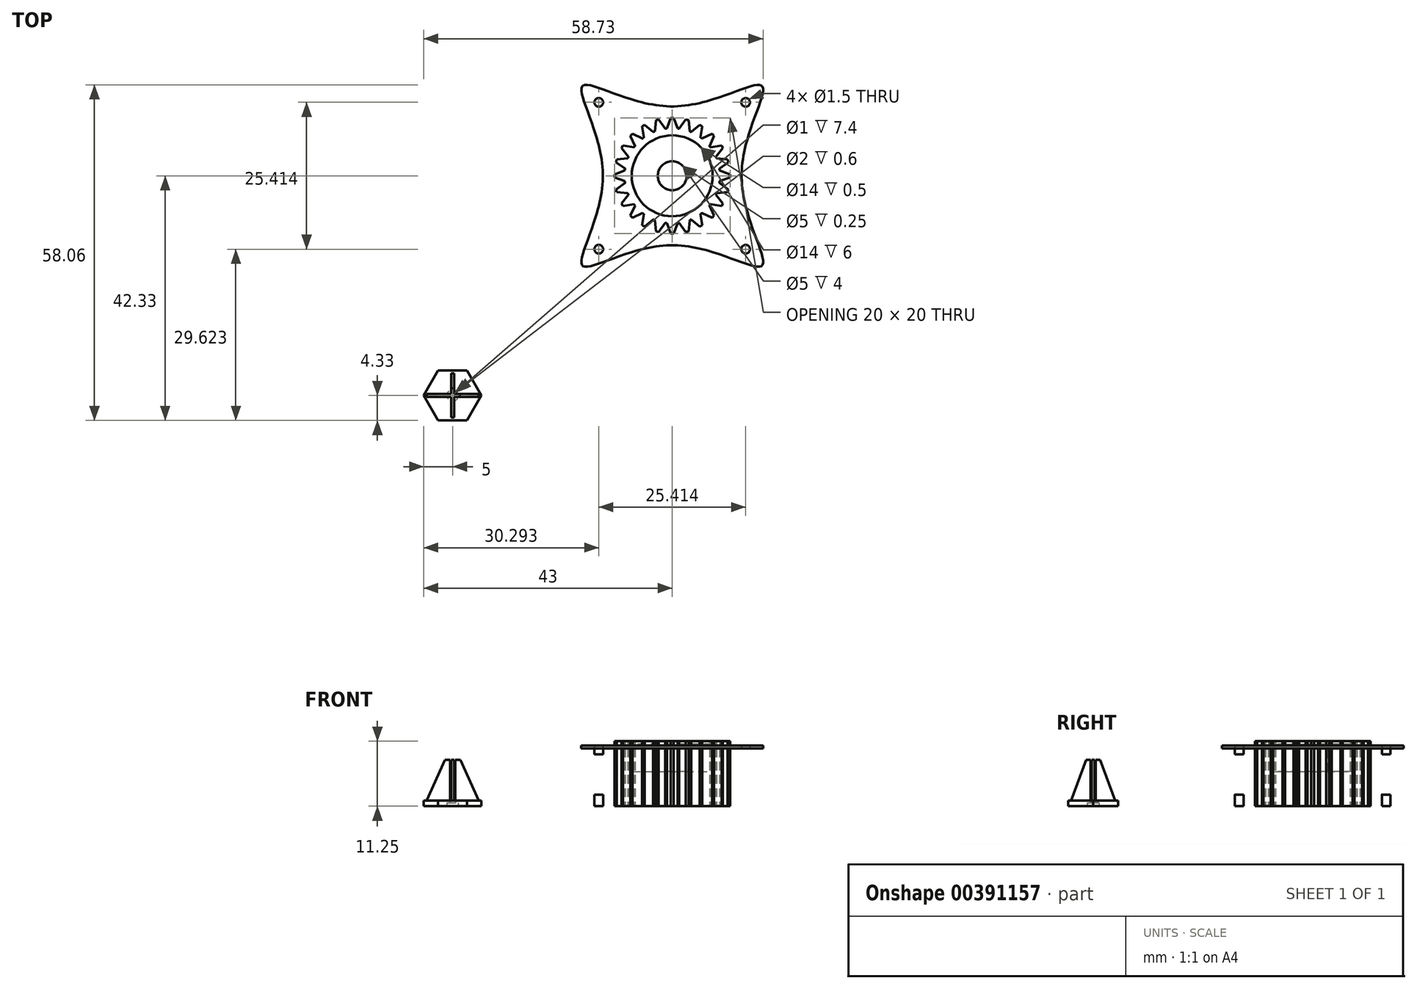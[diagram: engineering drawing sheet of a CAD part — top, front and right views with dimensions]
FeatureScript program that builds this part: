
annotation { "Feature Type Name" : "Feature", "Feature Type Description" : "" }
export const myFeature = defineFeature(function(context is Context, id is Id, definition is map)
    precondition{}
    {
        {
            var Q0;
            Q0=qCreatedBy(makeId("Top.planeOp"),FACE);
            var sketch = newSketch(context, id + "F0", { "sketchPlane" : qUnion([Q0])});
            skLineSegment(sketch, "E0.bottom", {"start": v(0, 0) * mm, "end": v(76, 0) * mm, "construction": true});
            skLineSegment(sketch, "E0.top", {"start": v(0, 76) * mm, "end": v(76, 76) * mm, "construction": true});
            skLineSegment(sketch, "E0.left", {"start": v(0, 0) * mm, "end": v(0, 76) * mm, "construction": true});
            skLineSegment(sketch, "E0.right", {"start": v(76, 0) * mm, "end": v(76, 76) * mm, "construction": true});
            skLineSegment(sketch, "E1", {"start": v(0, 0) * mm, "end": v(76, 76) * mm, "construction": true});
            skCircle(sketch, "E2", {"center": v(38, 38) * mm, "radius": 12 * mm, "construction": true});
            skLineSegment(sketch, "E3", {"start": v(0, 76) * mm, "end": v(76, 0) * mm, "construction": true});
            skLineSegment(sketch, "E4", {"start": v(38, 26) * mm, "end": v(50, 26) * mm, "construction": true});
            skLineSegment(sketch, "E5", {"start": v(50, 26) * mm, "end": v(50, 50) * mm, "construction": true});
            skLineSegment(sketch, "E6", {"start": v(50, 26) * mm, "end": v(53.54, 22.46) * mm, "construction": true});
            skLineSegment(sketch, "E7", {"start": v(53.54, 22.46) * mm, "end": v(53.54, 53.54) * mm, "construction": true});
            skLineSegment(sketch, "E8", {"start": v(53.54, 53.54) * mm, "end": v(22.46, 53.54) * mm, "construction": true});
            skLineSegment(sketch, "E9", {"start": v(22.46, 53.54) * mm, "end": v(22.46, 22.46) * mm, "construction": true});
            skLineSegment(sketch, "E10", {"start": v(22.46, 22.46) * mm, "end": v(53.54, 22.46) * mm, "construction": true});
            skPoint(sketch, "E11.7.internal.snap0", {"position": v(50, 38) * mm});
            skFitSpline(sketch, "E11", {"points": [v(22.46, 22.46) * mm, v(38, 26) * mm, v(53.54, 22.46) * mm, v(50, 38) * mm, v(53.54, 53.54) * mm, v(38, 50) * mm, v(22.46, 53.54) * mm, v(26, 38) * mm, v(22.46, 22.46) * mm]});
            skSolve(sketch);
        }
        {
            var Q0;
            Q0 = qSketchRegion(id + "F0", true);
            var Q1;
            Q1 = qConstructionFilter(qBodyType(qCreatedBy(id + "F0" ,EDGE), BodyType.WIRE), ConstructionObject.NO);
            extrude(context, id + "F1", {"entities" : qUnion([Q0]), "surfaceEntities" : qUnion([Q1]), "depth" : 2 * mm});
        }
        {
            var Q0;
            Q0=makeQuery(id+"F1.opExtrude","CAP_FACE",FACE,{"disambiguationData":[OSD([sQuery(id+"F0.wireOp",EDGE,"E11")])],"isStart":false});
            var sketch = newSketch(context, id + "F2", { "sketchPlane" : qUnion([Q0])});
            skLineSegment(sketch, "E12", {"start": v(0, 0) * mm, "end": v(38, 0) * mm, "construction": true});
            skLineSegment(sketch, "E13", {"start": v(38, 0) * mm, "end": v(38, 38) * mm, "construction": true});
            skCircle(sketch, "E14", {"center": v(38, 38) * mm, "radius": 10 * mm});
            skCircle(sketch, "E15", {"center": v(38, 38) * mm, "radius": 7 * mm});
            skLineSegment(sketch, "E16", {"start": v(38, 38) * mm, "end": v(22.46, 22.46) * mm, "construction": true});
            skLineSegment(sketch, "E17", {"start": v(30.94, 30.94) * mm, "end": v(31.3, 30.58) * mm, "construction": true});
            skLineSegment(sketch, "E18.MirrorCS", {"start": v(30.94, 30.94) * mm, "end": v(30.58, 31.3) * mm, "construction": true});
            skLineSegment(sketch, "E19", {"start": v(30.58, 31.3) * mm, "end": v(31.3, 30.58) * mm});
            skLineSegment(sketch, "E20", {"start": v(31.3, 30.58) * mm, "end": v(27.76, 27.05) * mm});
            skLineSegment(sketch, "E21", {"start": v(27.76, 27.05) * mm, "end": v(27.05, 27.76) * mm});
            skLineSegment(sketch, "E22", {"start": v(27.05, 27.76) * mm, "end": v(30.58, 31.3) * mm});
            skLineSegment(sketch, "E23", {"start": v(38, 38) * mm, "end": v(53.54, 22.46) * mm, "construction": true});
            skLineSegment(sketch, "E24", {"start": v(45.06, 30.94) * mm, "end": v(45.42, 31.3) * mm});
            skLineSegment(sketch, "E25", {"start": v(45.06, 30.94) * mm, "end": v(44.7, 30.58) * mm});
            skLineSegment(sketch, "E26", {"start": v(44.7, 30.58) * mm, "end": v(48.24, 27.05) * mm});
            skLineSegment(sketch, "E27", {"start": v(48.24, 27.05) * mm, "end": v(48.95, 27.76) * mm});
            skLineSegment(sketch, "E28", {"start": v(48.95, 27.76) * mm, "end": v(45.42, 31.3) * mm});
            skLineSegment(sketch, "E29", {"start": v(38, 38) * mm, "end": v(53.54, 53.54) * mm, "construction": true});
            skLineSegment(sketch, "E30", {"start": v(45.06, 45.06) * mm, "end": v(45.42, 44.7) * mm});
            skLineSegment(sketch, "E31", {"start": v(45.06, 45.06) * mm, "end": v(44.7, 45.42) * mm});
            skLineSegment(sketch, "E32", {"start": v(45.42, 44.7) * mm, "end": v(48.95, 48.24) * mm});
            skLineSegment(sketch, "E33", {"start": v(48.95, 48.24) * mm, "end": v(48.24, 48.95) * mm});
            skLineSegment(sketch, "E34", {"start": v(48.24, 48.95) * mm, "end": v(44.7, 45.42) * mm});
            skLineSegment(sketch, "E35", {"start": v(38, 38) * mm, "end": v(22.46, 53.54) * mm, "construction": true});
            skLineSegment(sketch, "E36", {"start": v(30.94, 45.06) * mm, "end": v(31.3, 45.42) * mm});
            skLineSegment(sketch, "E37", {"start": v(30.94, 45.06) * mm, "end": v(30.58, 44.7) * mm});
            skLineSegment(sketch, "E38", {"start": v(31.3, 45.42) * mm, "end": v(27.76, 48.95) * mm});
            skLineSegment(sketch, "E39", {"start": v(27.76, 48.95) * mm, "end": v(27.05, 48.24) * mm});
            skLineSegment(sketch, "E40", {"start": v(27.05, 48.24) * mm, "end": v(30.58, 44.7) * mm});
            skSolve(sketch);
        }
        {
            var Q0;
            Q0 = qSketchRegion(id + "F2", true);
            extrude(context, id + "F3", {"entities" : qUnion([Q0]), "operationType" : NewBodyOperationType.ADD, "depth" : 7 * mm});
        }
        {
            var Q0;
            Q0 = qSketchRegion(id + "F2", true);
            extrude(context, id + "F4", {"entities" : qUnion([Q0]), "operationType" : NewBodyOperationType.ADD, "depth" : 4 * mm});
        }
        {
            var Q0;
            Q0=makeQuery(id+"F3.opExtrude","SWEPT_FACE",FACE,{"disambiguationData":[OSD([sQuery(id+"F2.wireOp",EDGE,"E32")])]});
            var sketch = newSketch(context, id + "F5", { "sketchPlane" : qUnion([Q0])});
            skLineSegment(sketch, "E41", {"start": v(68.73, 2) * mm, "end": v(66.73, 2) * mm, "construction": true});
            skLineSegment(sketch, "E42", {"start": v(66.73, 2) * mm, "end": v(68.73, 9) * mm});
            skLineSegment(sketch, "E43", {"start": v(68.73, 9) * mm, "end": v(68.73, 2) * mm});
            skSolve(sketch);
        }
        {
            var Q0;
            {var subQ0=sQuery(id+"F5.wireOp",EDGE,"E42");Q0=makeQuery(id+"F5.imprint","IMPRINT",FACE,{"disambiguationData":[TD([[makeQuery(id+"F5.imprint","IMPRINT",EDGE,{"derivedFrom":subQ0}),-1.0]])]});}
            extrude(context, id + "F6", {"entities" : qUnion([Q0]), "operationType" : NewBodyOperationType.REMOVE, "oppositeDirection" : true, "depth" : 25 * mm});
        }
        {
            var Q0;
            Q0=makeQuery(id+"F3.opExtrude","SWEPT_FACE",FACE,{"disambiguationData":[OSD([sQuery(id+"F2.wireOp",EDGE,"E28")])]});
            var sketch = newSketch(context, id + "F7", { "sketchPlane" : qUnion([Q0])});
            skLineSegment(sketch, "E44", {"start": v(-14.99, 2) * mm, "end": v(-12.99, 2) * mm, "construction": true});
            skLineSegment(sketch, "E45", {"start": v(-12.99, 2) * mm, "end": v(-14.99, 9) * mm});
            skLineSegment(sketch, "E46", {"start": v(-14.99, 9) * mm, "end": v(-14.99, 2) * mm});
            skSolve(sketch);
        }
        {
            var Q0;
            {var subQ0=sQuery(id+"F7.wireOp",EDGE,"E45");Q0=makeQuery(id+"F7.imprint","IMPRINT",FACE,{"disambiguationData":[TD([[makeQuery(id+"F7.imprint","IMPRINT",EDGE,{"derivedFrom":subQ0}),1.0]])]});}
            extrude(context, id + "F8", {"entities" : qUnion([Q0]), "operationType" : NewBodyOperationType.REMOVE, "oppositeDirection" : true, "depth" : 25 * mm});
        }
        {
            var Q0;
            Q0=makeQuery(id+"F3.opExtrude","SWEPT_FACE",FACE,{"disambiguationData":[OSD([sQuery(id+"F2.wireOp",EDGE,"E38")])]});
            var sketch = newSketch(context, id + "F9", { "sketchPlane" : qUnion([Q0])});
            skLineSegment(sketch, "E47", {"start": v(14.99, 2) * mm, "end": v(12.99, 2) * mm, "construction": true});
            skLineSegment(sketch, "E48", {"start": v(12.99, 2) * mm, "end": v(14.99, 9) * mm});
            skLineSegment(sketch, "E49", {"start": v(14.99, 9) * mm, "end": v(14.99, 2) * mm});
            skSolve(sketch);
        }
        {
            var Q0;
            {var subQ0=sQuery(id+"F9.wireOp",EDGE,"E48");Q0=makeQuery(id+"F9.imprint","IMPRINT",FACE,{"disambiguationData":[TD([[makeQuery(id+"F9.imprint","IMPRINT",EDGE,{"derivedFrom":subQ0}),-1.0]])]});}
            extrude(context, id + "F10", {"entities" : qUnion([Q0]), "operationType" : NewBodyOperationType.REMOVE, "oppositeDirection" : true, "depth" : 25 * mm});
        }
        {
            var Q0;
            Q0=makeQuery(id+"F3.opExtrude","SWEPT_FACE",FACE,{"disambiguationData":[OSD([sQuery(id+"F2.wireOp",EDGE,"E22")])]});
            var sketch = newSketch(context, id + "F11", { "sketchPlane" : qUnion([Q0])});
            skLineSegment(sketch, "E50", {"start": v(-38.75, 2) * mm, "end": v(-40.75, 2) * mm, "construction": true});
            skLineSegment(sketch, "E51", {"start": v(-40.75, 2) * mm, "end": v(-38.75, 9) * mm});
            skLineSegment(sketch, "E52", {"start": v(-38.75, 9) * mm, "end": v(-38.75, 2) * mm});
            skSolve(sketch);
        }
        {
            var Q0;
            {var subQ0=sQuery(id+"F11.wireOp",EDGE,"E51");Q0=makeQuery(id+"F11.imprint","IMPRINT",FACE,{"disambiguationData":[TD([[makeQuery(id+"F11.imprint","IMPRINT",EDGE,{"derivedFrom":subQ0}),-1.0]])]});}
            extrude(context, id + "F12", {"entities" : qUnion([Q0]), "operationType" : NewBodyOperationType.REMOVE, "oppositeDirection" : true, "depth" : 25 * mm});
        }
        {
            var Q0;
            {var subQ0=sQuery(id+"F2.wireOp",EDGE,"E22");var subQ1=sQuery(id+"F2.wireOp",EDGE,"E38");var subQ2=sQuery(id+"F2.wireOp",EDGE,"E28");var subQ3=sQuery(id+"F2.wireOp",EDGE,"E32");var subQ7=sQuery(id+"F0.wireOp",EDGE,"E11");Q0=makeQuery(id+"F12.boolean.opBoolean","MERGE",FACE,{"derivedFrom":[makeQuery(id+"F10.boolean.opBoolean","MERGE",FACE,{"derivedFrom":[makeQuery(id+"F8.boolean.opBoolean","MERGE",FACE,{"derivedFrom":[makeQuery(id+"F6.boolean.opBoolean","MERGE",FACE,{"derivedFrom":[makeQuery(id+"F3.boolean.opBoolean","SPLIT",FACE,{"disambiguationData":[TD([makeQuery(id+"F1.opExtrude","SWEPT_FACE",FACE,{"disambiguationData":[OSD([subQ7])]})])],"derivedFrom":makeQuery(id+"F1.opExtrude","CAP_FACE",FACE,{"disambiguationData":[OSD([subQ7])],"isStart":false})}),makeQuery(id+"F6.opExtrude","SWEPT_FACE",FACE,{"disambiguationData":[OSD([subQ3])]})]}),makeQuery(id+"F8.opExtrude","SWEPT_FACE",FACE,{"disambiguationData":[OSD([subQ2])]})]}),makeQuery(id+"F10.opExtrude","SWEPT_FACE",FACE,{"disambiguationData":[OSD([subQ1])]})]}),makeQuery(id+"F12.opExtrude","SWEPT_FACE",FACE,{"disambiguationData":[OSD([subQ0])]})]});}
            var sketch = newSketch(context, id + "F13", { "sketchPlane" : qUnion([Q0])});
            skLineSegment(sketch, "E53", {"start": v(38, 38) * mm, "end": v(38, 26) * mm, "construction": true});
            skLineSegment(sketch, "E54", {"start": v(38, 38) * mm, "end": v(50, 38) * mm, "construction": true});
            skLineSegment(sketch, "E55", {"start": v(38, 38) * mm, "end": v(38, 50) * mm, "construction": true});
            skLineSegment(sketch, "E56", {"start": v(38, 38) * mm, "end": v(26, 38) * mm, "construction": true});
            skLineSegment(sketch, "E57", {"start": v(38, 38) * mm, "end": v(53.54, 22.46) * mm, "construction": true});
            skLineSegment(sketch, "E58", {"start": v(38, 38) * mm, "end": v(53.54, 53.54) * mm, "construction": true});
            skLineSegment(sketch, "E59", {"start": v(38, 38) * mm, "end": v(22.46, 53.54) * mm, "construction": true});
            skLineSegment(sketch, "E60", {"start": v(38, 38) * mm, "end": v(22.46, 22.46) * mm, "construction": true});
            skFitSpline(sketch, "E61", {"points": [v(38, 26) * mm, v(53.54, 22.46) * mm, v(50, 38) * mm, v(53.54, 53.54) * mm, v(38, 50) * mm, v(22.46, 53.54) * mm, v(26, 38) * mm, v(22.46, 22.46) * mm, v(38, 26) * mm]});
            skSolve(sketch);
        }
        {
            var Q0;
            Q0 = qSketchRegion(id + "F13", true);
            extrude(context, id + "F14", {"entities" : qUnion([Q0]), "operationType" : NewBodyOperationType.ADD, "depth" : 8 * mm, "hasSecondDirection" : true, "secondDirectionOppositeDirection" : false, "secondDirectionDepth" : 7 * mm});
        }
        {
            var Q0;
            Q0=makeQuery(id+"F14.opExtrude","CAP_FACE",FACE,{"disambiguationData":[OSD([sQuery(id+"F13.wireOp",EDGE,"E61")])],"isStart":false});
            var sketch = newSketch(context, id + "F15", { "sketchPlane" : qUnion([Q0])});
            skLineSegment(sketch, "E62", {"start": v(0, 0) * mm, "end": v(38, 0) * mm, "construction": true});
            skLineSegment(sketch, "E63", {"start": v(38, 0) * mm, "end": v(38, 38) * mm, "construction": true});
            skCircle(sketch, "E64", {"center": v(38, 38) * mm, "radius": 10 * mm, "construction": true});
            skLineSegment(sketch, "E65", {"start": v(38, 28) * mm, "end": v(38.25, 28) * mm});
            skLineSegment(sketch, "E66", {"start": v(37.75, 28) * mm, "end": v(38, 28) * mm});
            skLineSegment(sketch, "E67", {"start": v(38.93, 29.8) * mm, "end": v(38.25, 28) * mm});
            skLineSegment(sketch, "E68.MirrorCS", {"start": v(37.07, 29.8) * mm, "end": v(37.75, 28) * mm});
            skLineSegment(sketch, "E69.1.2", {"start": v(34.98, 30.32) * mm, "end": v(35.17, 28.4) * mm});
            skLineSegment(sketch, "E69.1.3", {"start": v(35.17, 28.4) * mm, "end": v(35.41, 28.34) * mm});
            skLineSegment(sketch, "E69.1.4", {"start": v(35.41, 28.34) * mm, "end": v(35.65, 28.28) * mm});
            skLineSegment(sketch, "E69.1.5", {"start": v(36.77, 29.84) * mm, "end": v(35.65, 28.28) * mm});
            skLineSegment(sketch, "E69.2.2", {"start": v(33.1, 31.36) * mm, "end": v(32.78, 29.46) * mm});
            skLineSegment(sketch, "E69.2.3", {"start": v(32.78, 29.46) * mm, "end": v(33, 29.34) * mm});
            skLineSegment(sketch, "E69.2.4", {"start": v(33, 29.34) * mm, "end": v(33.22, 29.21) * mm});
            skLineSegment(sketch, "E69.2.5", {"start": v(34.7, 30.44) * mm, "end": v(33.22, 29.21) * mm});
            skLineSegment(sketch, "E69.3.2", {"start": v(31.55, 32.86) * mm, "end": v(30.75, 31.1) * mm});
            skLineSegment(sketch, "E69.3.3", {"start": v(30.75, 31.1) * mm, "end": v(30.93, 30.93) * mm});
            skLineSegment(sketch, "E69.3.4", {"start": v(30.93, 30.93) * mm, "end": v(31.1, 30.75) * mm});
            skLineSegment(sketch, "E69.3.5", {"start": v(32.86, 31.55) * mm, "end": v(31.1, 30.75) * mm});
            skLineSegment(sketch, "E69.4.2", {"start": v(30.44, 34.7) * mm, "end": v(29.21, 33.22) * mm});
            skLineSegment(sketch, "E69.4.3", {"start": v(29.21, 33.22) * mm, "end": v(29.34, 33) * mm});
            skLineSegment(sketch, "E69.4.4", {"start": v(29.34, 33) * mm, "end": v(29.46, 32.78) * mm});
            skLineSegment(sketch, "E69.4.5", {"start": v(31.36, 33.1) * mm, "end": v(29.46, 32.78) * mm});
            skLineSegment(sketch, "E69.5.2", {"start": v(29.84, 36.77) * mm, "end": v(28.28, 35.65) * mm});
            skLineSegment(sketch, "E69.5.3", {"start": v(28.28, 35.65) * mm, "end": v(28.34, 35.41) * mm});
            skLineSegment(sketch, "E69.5.4", {"start": v(28.34, 35.41) * mm, "end": v(28.4, 35.17) * mm});
            skLineSegment(sketch, "E69.5.5", {"start": v(30.32, 34.98) * mm, "end": v(28.4, 35.17) * mm});
            skLineSegment(sketch, "E69.6.2", {"start": v(29.8, 38.93) * mm, "end": v(28, 38.25) * mm});
            skLineSegment(sketch, "E69.6.3", {"start": v(28, 38.25) * mm, "end": v(28, 38) * mm});
            skLineSegment(sketch, "E69.6.4", {"start": v(28, 38) * mm, "end": v(28, 37.75) * mm});
            skLineSegment(sketch, "E69.6.5", {"start": v(29.8, 37.07) * mm, "end": v(28, 37.75) * mm});
            skLineSegment(sketch, "E69.7.2", {"start": v(30.32, 41.02) * mm, "end": v(28.4, 40.83) * mm});
            skLineSegment(sketch, "E69.7.3", {"start": v(28.4, 40.83) * mm, "end": v(28.34, 40.59) * mm});
            skLineSegment(sketch, "E69.7.4", {"start": v(28.34, 40.59) * mm, "end": v(28.28, 40.35) * mm});
            skLineSegment(sketch, "E69.7.5", {"start": v(29.84, 39.23) * mm, "end": v(28.28, 40.35) * mm});
            skLineSegment(sketch, "E69.8.2", {"start": v(31.36, 42.9) * mm, "end": v(29.46, 43.22) * mm});
            skLineSegment(sketch, "E69.8.3", {"start": v(29.46, 43.22) * mm, "end": v(29.34, 43) * mm});
            skLineSegment(sketch, "E69.8.4", {"start": v(29.34, 43) * mm, "end": v(29.21, 42.78) * mm});
            skLineSegment(sketch, "E69.8.5", {"start": v(30.44, 41.3) * mm, "end": v(29.21, 42.78) * mm});
            skLineSegment(sketch, "E69.9.2", {"start": v(32.86, 44.45) * mm, "end": v(31.1, 45.25) * mm});
            skLineSegment(sketch, "E69.9.3", {"start": v(31.1, 45.25) * mm, "end": v(30.93, 45.07) * mm});
            skLineSegment(sketch, "E69.9.4", {"start": v(30.93, 45.07) * mm, "end": v(30.75, 44.9) * mm});
            skLineSegment(sketch, "E69.9.5", {"start": v(31.55, 43.14) * mm, "end": v(30.75, 44.9) * mm});
            skLineSegment(sketch, "E69.10.2", {"start": v(34.7, 45.56) * mm, "end": v(33.22, 46.79) * mm});
            skLineSegment(sketch, "E69.10.3", {"start": v(33.22, 46.79) * mm, "end": v(33, 46.66) * mm});
            skLineSegment(sketch, "E69.10.4", {"start": v(33, 46.66) * mm, "end": v(32.78, 46.54) * mm});
            skLineSegment(sketch, "E69.10.5", {"start": v(33.1, 44.64) * mm, "end": v(32.78, 46.54) * mm});
            skLineSegment(sketch, "E69.11.2", {"start": v(36.77, 46.16) * mm, "end": v(35.65, 47.72) * mm});
            skLineSegment(sketch, "E69.11.3", {"start": v(35.65, 47.72) * mm, "end": v(35.41, 47.66) * mm});
            skLineSegment(sketch, "E69.11.4", {"start": v(35.41, 47.66) * mm, "end": v(35.17, 47.6) * mm});
            skLineSegment(sketch, "E69.11.5", {"start": v(34.98, 45.68) * mm, "end": v(35.17, 47.6) * mm});
            skLineSegment(sketch, "E69.12.2", {"start": v(38.93, 46.2) * mm, "end": v(38.25, 48) * mm});
            skLineSegment(sketch, "E69.12.3", {"start": v(38.25, 48) * mm, "end": v(38, 48) * mm});
            skLineSegment(sketch, "E69.12.4", {"start": v(38, 48) * mm, "end": v(37.75, 48) * mm});
            skLineSegment(sketch, "E69.12.5", {"start": v(37.07, 46.2) * mm, "end": v(37.75, 48) * mm});
            skLineSegment(sketch, "E69.13.2", {"start": v(41.02, 45.68) * mm, "end": v(40.83, 47.6) * mm});
            skLineSegment(sketch, "E69.13.3", {"start": v(40.83, 47.6) * mm, "end": v(40.59, 47.66) * mm});
            skLineSegment(sketch, "E69.13.4", {"start": v(40.59, 47.66) * mm, "end": v(40.35, 47.72) * mm});
            skLineSegment(sketch, "E69.13.5", {"start": v(39.23, 46.16) * mm, "end": v(40.35, 47.72) * mm});
            skLineSegment(sketch, "E69.14.2", {"start": v(42.9, 44.64) * mm, "end": v(43.22, 46.54) * mm});
            skLineSegment(sketch, "E69.14.3", {"start": v(43.22, 46.54) * mm, "end": v(43, 46.66) * mm});
            skLineSegment(sketch, "E69.14.4", {"start": v(43, 46.66) * mm, "end": v(42.78, 46.79) * mm});
            skLineSegment(sketch, "E69.14.5", {"start": v(41.3, 45.56) * mm, "end": v(42.78, 46.79) * mm});
            skLineSegment(sketch, "E69.15.2", {"start": v(44.45, 43.14) * mm, "end": v(45.25, 44.9) * mm});
            skLineSegment(sketch, "E69.15.3", {"start": v(45.25, 44.9) * mm, "end": v(45.07, 45.07) * mm});
            skLineSegment(sketch, "E69.15.4", {"start": v(45.07, 45.07) * mm, "end": v(44.9, 45.25) * mm});
            skLineSegment(sketch, "E69.15.5", {"start": v(43.14, 44.45) * mm, "end": v(44.9, 45.25) * mm});
            skLineSegment(sketch, "E69.16.2", {"start": v(45.56, 41.3) * mm, "end": v(46.79, 42.78) * mm});
            skLineSegment(sketch, "E69.16.3", {"start": v(46.79, 42.78) * mm, "end": v(46.66, 43) * mm});
            skLineSegment(sketch, "E69.16.4", {"start": v(46.66, 43) * mm, "end": v(46.54, 43.22) * mm});
            skLineSegment(sketch, "E69.16.5", {"start": v(44.64, 42.9) * mm, "end": v(46.54, 43.22) * mm});
            skLineSegment(sketch, "E69.17.2", {"start": v(46.16, 39.23) * mm, "end": v(47.72, 40.35) * mm});
            skLineSegment(sketch, "E69.17.3", {"start": v(47.72, 40.35) * mm, "end": v(47.66, 40.59) * mm});
            skLineSegment(sketch, "E69.17.4", {"start": v(47.66, 40.59) * mm, "end": v(47.6, 40.83) * mm});
            skLineSegment(sketch, "E69.17.5", {"start": v(45.68, 41.02) * mm, "end": v(47.6, 40.83) * mm});
            skLineSegment(sketch, "E69.18.2", {"start": v(46.2, 37.07) * mm, "end": v(48, 37.75) * mm});
            skLineSegment(sketch, "E69.18.3", {"start": v(48, 37.75) * mm, "end": v(48, 38) * mm});
            skLineSegment(sketch, "E69.18.4", {"start": v(48, 38) * mm, "end": v(48, 38.25) * mm});
            skLineSegment(sketch, "E69.18.5", {"start": v(46.2, 38.93) * mm, "end": v(48, 38.25) * mm});
            skLineSegment(sketch, "E69.19.2", {"start": v(45.68, 34.98) * mm, "end": v(47.6, 35.17) * mm});
            skLineSegment(sketch, "E69.19.3", {"start": v(47.6, 35.17) * mm, "end": v(47.66, 35.41) * mm});
            skLineSegment(sketch, "E69.19.4", {"start": v(47.66, 35.41) * mm, "end": v(47.72, 35.65) * mm});
            skLineSegment(sketch, "E69.19.5", {"start": v(46.16, 36.77) * mm, "end": v(47.72, 35.65) * mm});
            skLineSegment(sketch, "E69.anchor1", {"start": v(38, 38) * mm, "end": v(38, 30) * mm, "construction": true});
            skLineSegment(sketch, "E69.anchor2", {"start": v(38, 38) * mm, "end": v(38, 30) * mm, "construction": true});
            skLineSegment(sketch, "E70.6.20.0", {"start": v(44.64, 33.1) * mm, "end": v(46.54, 32.78) * mm});
            skLineSegment(sketch, "E70.9.20.0", {"start": v(46.54, 32.78) * mm, "end": v(46.66, 33) * mm});
            skLineSegment(sketch, "E70.12.20.0", {"start": v(46.66, 33) * mm, "end": v(46.79, 33.22) * mm});
            skLineSegment(sketch, "E70.15.20.0", {"start": v(45.56, 34.7) * mm, "end": v(46.79, 33.22) * mm});
            skLineSegment(sketch, "E70.6.21.0", {"start": v(43.14, 31.55) * mm, "end": v(44.9, 30.75) * mm});
            skLineSegment(sketch, "E70.9.21.0", {"start": v(44.9, 30.75) * mm, "end": v(45.07, 30.93) * mm});
            skLineSegment(sketch, "E70.12.21.0", {"start": v(45.07, 30.93) * mm, "end": v(45.25, 31.1) * mm});
            skLineSegment(sketch, "E70.15.21.0", {"start": v(44.45, 32.86) * mm, "end": v(45.25, 31.1) * mm});
            skLineSegment(sketch, "E70.6.22.0", {"start": v(41.3, 30.44) * mm, "end": v(42.78, 29.21) * mm});
            skLineSegment(sketch, "E70.9.22.0", {"start": v(42.78, 29.21) * mm, "end": v(43, 29.34) * mm});
            skLineSegment(sketch, "E70.12.22.0", {"start": v(43, 29.34) * mm, "end": v(43.22, 29.46) * mm});
            skLineSegment(sketch, "E70.15.22.0", {"start": v(42.9, 31.36) * mm, "end": v(43.22, 29.46) * mm});
            skLineSegment(sketch, "E70.6.23.0", {"start": v(39.23, 29.84) * mm, "end": v(40.35, 28.28) * mm});
            skLineSegment(sketch, "E70.9.23.0", {"start": v(40.35, 28.28) * mm, "end": v(40.59, 28.34) * mm});
            skLineSegment(sketch, "E70.12.23.0", {"start": v(40.59, 28.34) * mm, "end": v(40.83, 28.4) * mm});
            skLineSegment(sketch, "E70.15.23.0", {"start": v(41.02, 30.32) * mm, "end": v(40.83, 28.4) * mm});
            skArc(sketch, "E71", {"start": v(34.7, 30.44) * mm, "mid": v(34.84, 30.38) * mm, "end": v(34.98, 30.32) * mm});
            skPoint(sketch, "E72.orphan", {"position": v(30, 37) * mm});
            skPoint(sketch, "E73.orphan", {"position": v(30.01, 36.9) * mm});
            skPoint(sketch, "E74.orphan", {"position": v(30.57, 34.87) * mm});
            skPoint(sketch, "E75.orphan", {"position": v(31.57, 33.13) * mm});
            skPoint(sketch, "E76.orphan", {"position": v(31.64, 33.05) * mm});
            skPoint(sketch, "E77.orphan", {"position": v(33.05, 31.64) * mm});
            skPoint(sketch, "E78.orphan", {"position": v(33.13, 31.57) * mm});
            skArc(sketch, "E79.trimOffspring", {"start": v(32.86, 31.55) * mm, "mid": v(32.98, 31.45) * mm, "end": v(33.1, 31.36) * mm});
            skArc(sketch, "E80.trimOffspring", {"start": v(31.36, 33.1) * mm, "mid": v(31.45, 32.98) * mm, "end": v(31.55, 32.86) * mm});
            skArc(sketch, "E81.trimOffspring", {"start": v(36.77, 29.84) * mm, "mid": v(36.92, 29.82) * mm, "end": v(37.07, 29.8) * mm});
            skPoint(sketch, "E82.orphan", {"position": v(36.9, 30.01) * mm});
            skPoint(sketch, "E83.orphan", {"position": v(37, 30) * mm});
            skPoint(sketch, "E84.MirrorCS.start.orphan", {"position": v(38, 30) * mm});
            skPoint(sketch, "E85.orphan", {"position": v(34.96, 30.53) * mm});
            skPoint(sketch, "E86.orphan", {"position": v(34.87, 30.57) * mm});
            skArc(sketch, "E87.trimOffspring", {"start": v(38.93, 29.8) * mm, "mid": v(39.08, 29.82) * mm, "end": v(39.23, 29.84) * mm});
            skArc(sketch, "E88.trimOffspring", {"start": v(30.32, 34.98) * mm, "mid": v(30.38, 34.84) * mm, "end": v(30.44, 34.7) * mm});
            skArc(sketch, "E89.trimOffspring", {"start": v(29.8, 37.07) * mm, "mid": v(29.82, 36.92) * mm, "end": v(29.84, 36.77) * mm});
            skArc(sketch, "E90.trimOffspring", {"start": v(41.02, 30.32) * mm, "mid": v(41.16, 30.38) * mm, "end": v(41.3, 30.44) * mm});
            skPoint(sketch, "E91.orphan", {"position": v(39.1, 30.01) * mm});
            skPoint(sketch, "E92.orphan", {"position": v(39, 30) * mm});
            skPoint(sketch, "E93.orphan", {"position": v(41.13, 30.57) * mm});
            skPoint(sketch, "E94.orphan", {"position": v(41.04, 30.53) * mm});
            skPoint(sketch, "E95.orphan", {"position": v(42.87, 31.57) * mm});
            skPoint(sketch, "E96.orphan", {"position": v(42.95, 31.64) * mm});
            skPoint(sketch, "E97.orphan", {"position": v(44.36, 33.05) * mm});
            skPoint(sketch, "E98.orphan", {"position": v(44.43, 33.13) * mm});
            skPoint(sketch, "E99.orphan", {"position": v(45.43, 34.87) * mm});
            skPoint(sketch, "E100.orphan", {"position": v(45.47, 34.96) * mm});
            skPoint(sketch, "E101.orphan", {"position": v(45.99, 36.9) * mm});
            skPoint(sketch, "E102.orphan", {"position": v(46, 37) * mm});
            skPoint(sketch, "E103.orphan", {"position": v(46, 39) * mm});
            skPoint(sketch, "E104.orphan", {"position": v(45.99, 39.1) * mm});
            skPoint(sketch, "E105.orphan", {"position": v(45.47, 41.04) * mm});
            skPoint(sketch, "E106.orphan", {"position": v(45.43, 41.13) * mm});
            skPoint(sketch, "E107.orphan", {"position": v(44.43, 42.87) * mm});
            skPoint(sketch, "E108.orphan", {"position": v(44.36, 42.95) * mm});
            skPoint(sketch, "E109.orphan", {"position": v(42.95, 44.36) * mm});
            skPoint(sketch, "E110.orphan", {"position": v(42.87, 44.43) * mm});
            skArc(sketch, "E111.trimOffspring", {"start": v(44.45, 32.86) * mm, "mid": v(44.55, 32.98) * mm, "end": v(44.64, 33.1) * mm});
            skArc(sketch, "E112.trimOffspring", {"start": v(46.16, 36.77) * mm, "mid": v(46.18, 36.92) * mm, "end": v(46.2, 37.07) * mm});
            skArc(sketch, "E113.trimOffspring", {"start": v(45.68, 41.02) * mm, "mid": v(45.62, 41.16) * mm, "end": v(45.56, 41.3) * mm});
            skArc(sketch, "E114.trimOffspring", {"start": v(44.64, 42.9) * mm, "mid": v(44.55, 43.02) * mm, "end": v(44.45, 43.14) * mm});
            skArc(sketch, "E115.trimOffspring", {"start": v(46.2, 38.93) * mm, "mid": v(46.18, 39.08) * mm, "end": v(46.16, 39.23) * mm});
            skArc(sketch, "E116.trimOffspring", {"start": v(43.14, 44.45) * mm, "mid": v(43.02, 44.55) * mm, "end": v(42.9, 44.64) * mm});
            skArc(sketch, "E117.trimOffspring", {"start": v(41.3, 45.56) * mm, "mid": v(41.16, 45.62) * mm, "end": v(41.02, 45.68) * mm});
            skPoint(sketch, "E118.orphan", {"position": v(41.04, 45.47) * mm});
            skArc(sketch, "E119.trimOffspring", {"start": v(39.23, 46.16) * mm, "mid": v(39.08, 46.18) * mm, "end": v(38.93, 46.2) * mm});
            skPoint(sketch, "E120.orphan", {"position": v(39.1, 45.99) * mm});
            skPoint(sketch, "E121.orphan", {"position": v(39, 46) * mm});
            skArc(sketch, "E122.trimOffspring", {"start": v(37.07, 46.2) * mm, "mid": v(36.92, 46.18) * mm, "end": v(36.77, 46.16) * mm});
            skPoint(sketch, "E123.orphan", {"position": v(37, 46) * mm});
            skPoint(sketch, "E124.orphan", {"position": v(36.9, 45.99) * mm});
            skArc(sketch, "E125.trimOffspring", {"start": v(34.98, 45.68) * mm, "mid": v(34.84, 45.62) * mm, "end": v(34.7, 45.56) * mm});
            skPoint(sketch, "E126.orphan", {"position": v(34.96, 45.47) * mm});
            skPoint(sketch, "E127.orphan", {"position": v(34.87, 45.43) * mm});
            skPoint(sketch, "E128.orphan", {"position": v(33.13, 44.43) * mm});
            skPoint(sketch, "E129.orphan", {"position": v(33.05, 44.36) * mm});
            skPoint(sketch, "E130.orphan", {"position": v(31.64, 42.95) * mm});
            skPoint(sketch, "E131.orphan", {"position": v(31.57, 42.87) * mm});
            skArc(sketch, "E132.trimOffspring", {"start": v(33.1, 44.64) * mm, "mid": v(32.98, 44.55) * mm, "end": v(32.86, 44.45) * mm});
            skArc(sketch, "E133.trimOffspring", {"start": v(31.55, 43.14) * mm, "mid": v(31.45, 43.02) * mm, "end": v(31.36, 42.9) * mm});
            skArc(sketch, "E134.trimOffspring", {"start": v(30.44, 41.3) * mm, "mid": v(30.38, 41.16) * mm, "end": v(30.32, 41.02) * mm});
            skPoint(sketch, "E135.orphan", {"position": v(30.57, 41.13) * mm});
            skPoint(sketch, "E136.orphan", {"position": v(30.53, 41.04) * mm});
            skArc(sketch, "E137.trimOffspring", {"start": v(29.84, 39.23) * mm, "mid": v(29.82, 39.08) * mm, "end": v(29.8, 38.93) * mm});
            skPoint(sketch, "E138.orphan", {"position": v(30, 39) * mm});
            skPoint(sketch, "E139.orphan", {"position": v(30.01, 39.1) * mm});
            skArc(sketch, "E140", {"start": v(42.9, 31.36) * mm, "mid": v(43.02, 31.45) * mm, "end": v(43.14, 31.55) * mm});
            skArc(sketch, "E141", {"start": v(45.56, 34.7) * mm, "mid": v(45.62, 34.84) * mm, "end": v(45.68, 34.98) * mm});
            skSolve(sketch);
        }
        {
            var Q0;
            Q0=makeQuery(id+"F15.imprint","IMPRINT",FACE,{"disambiguationData":[TD([[makeQuery(id+"F15.imprint","IMPRINT",EDGE,{"derivedFrom":sQuery(id+"F15.wireOp",EDGE,"E69.1.2")}),1.0]])]});
            extrude(context, id + "F16", {"entities" : qUnion([Q0]), "operationType" : NewBodyOperationType.ADD, "depth" : 1.25 * mm});
        }
        {
            var Q0;
            Q0=makeQuery(id+"F16.opExtrude","CAP_FACE",FACE,{"disambiguationData":[OSD([sQuery(id+"F15.wireOp",EDGE,"E69.1.2"),sQuery(id+"F15.wireOp",EDGE,"E69.1.3"),sQuery(id+"F15.wireOp",EDGE,"E69.1.4"),sQuery(id+"F15.wireOp",EDGE,"E69.1.5"),sQuery(id+"F15.wireOp",EDGE,"E69.2.2"),sQuery(id+"F15.wireOp",EDGE,"E69.2.3"),sQuery(id+"F15.wireOp",EDGE,"E69.2.4"),sQuery(id+"F15.wireOp",EDGE,"E69.2.5"),sQuery(id+"F15.wireOp",EDGE,"E69.3.2"),sQuery(id+"F15.wireOp",EDGE,"E69.3.3"),sQuery(id+"F15.wireOp",EDGE,"E69.3.4"),sQuery(id+"F15.wireOp",EDGE,"E69.3.5"),sQuery(id+"F15.wireOp",EDGE,"E69.4.2"),sQuery(id+"F15.wireOp",EDGE,"E69.4.3"),sQuery(id+"F15.wireOp",EDGE,"E69.4.4"),sQuery(id+"F15.wireOp",EDGE,"E69.4.5"),sQuery(id+"F15.wireOp",EDGE,"E69.5.2"),sQuery(id+"F15.wireOp",EDGE,"E69.5.3"),sQuery(id+"F15.wireOp",EDGE,"E69.5.4"),sQuery(id+"F15.wireOp",EDGE,"E69.5.5"),sQuery(id+"F15.wireOp",EDGE,"E69.6.2"),sQuery(id+"F15.wireOp",EDGE,"E69.6.3"),sQuery(id+"F15.wireOp",EDGE,"E69.6.4"),sQuery(id+"F15.wireOp",EDGE,"E69.6.5"),sQuery(id+"F15.wireOp",EDGE,"E69.7.2"),sQuery(id+"F15.wireOp",EDGE,"E69.7.3"),sQuery(id+"F15.wireOp",EDGE,"E69.7.4"),sQuery(id+"F15.wireOp",EDGE,"E69.7.5"),sQuery(id+"F15.wireOp",EDGE,"E69.8.2"),sQuery(id+"F15.wireOp",EDGE,"E69.8.3"),sQuery(id+"F15.wireOp",EDGE,"E69.8.4"),sQuery(id+"F15.wireOp",EDGE,"E69.8.5"),sQuery(id+"F15.wireOp",EDGE,"E69.9.2"),sQuery(id+"F15.wireOp",EDGE,"E69.9.3"),sQuery(id+"F15.wireOp",EDGE,"E69.9.4"),sQuery(id+"F15.wireOp",EDGE,"E69.9.5"),sQuery(id+"F15.wireOp",EDGE,"E69.10.2"),sQuery(id+"F15.wireOp",EDGE,"E69.10.3"),sQuery(id+"F15.wireOp",EDGE,"E69.10.4"),sQuery(id+"F15.wireOp",EDGE,"E69.10.5"),sQuery(id+"F15.wireOp",EDGE,"E69.11.2"),sQuery(id+"F15.wireOp",EDGE,"E69.11.3"),sQuery(id+"F15.wireOp",EDGE,"E69.11.4"),sQuery(id+"F15.wireOp",EDGE,"E69.11.5"),sQuery(id+"F15.wireOp",EDGE,"E69.12.2"),sQuery(id+"F15.wireOp",EDGE,"E69.12.3"),sQuery(id+"F15.wireOp",EDGE,"E69.12.4"),sQuery(id+"F15.wireOp",EDGE,"E69.12.5"),sQuery(id+"F15.wireOp",EDGE,"E69.13.2"),sQuery(id+"F15.wireOp",EDGE,"E69.13.3"),sQuery(id+"F15.wireOp",EDGE,"E69.13.4"),sQuery(id+"F15.wireOp",EDGE,"E69.13.5"),sQuery(id+"F15.wireOp",EDGE,"E69.14.2"),sQuery(id+"F15.wireOp",EDGE,"E69.14.3"),sQuery(id+"F15.wireOp",EDGE,"E69.14.4"),sQuery(id+"F15.wireOp",EDGE,"E69.14.5"),sQuery(id+"F15.wireOp",EDGE,"E69.15.2"),sQuery(id+"F15.wireOp",EDGE,"E69.15.3"),sQuery(id+"F15.wireOp",EDGE,"E69.15.4"),sQuery(id+"F15.wireOp",EDGE,"E69.15.5"),sQuery(id+"F15.wireOp",EDGE,"E69.16.2"),sQuery(id+"F15.wireOp",EDGE,"E69.16.3"),sQuery(id+"F15.wireOp",EDGE,"E69.16.4"),sQuery(id+"F15.wireOp",EDGE,"E69.16.5"),sQuery(id+"F15.wireOp",EDGE,"E69.17.2"),sQuery(id+"F15.wireOp",EDGE,"E69.17.3"),sQuery(id+"F15.wireOp",EDGE,"E69.17.4"),sQuery(id+"F15.wireOp",EDGE,"E69.17.5"),sQuery(id+"F15.wireOp",EDGE,"E69.18.2"),sQuery(id+"F15.wireOp",EDGE,"E69.18.3"),sQuery(id+"F15.wireOp",EDGE,"E69.18.4"),sQuery(id+"F15.wireOp",EDGE,"E69.18.5"),sQuery(id+"F15.wireOp",EDGE,"E69.19.2"),sQuery(id+"F15.wireOp",EDGE,"E69.19.3"),sQuery(id+"F15.wireOp",EDGE,"E69.19.4"),sQuery(id+"F15.wireOp",EDGE,"E69.19.5"),sQuery(id+"F15.wireOp",EDGE,"E70.6.20.0"),sQuery(id+"F15.wireOp",EDGE,"E70.9.20.0"),sQuery(id+"F15.wireOp",EDGE,"E70.12.20.0"),sQuery(id+"F15.wireOp",EDGE,"E70.15.20.0"),sQuery(id+"F15.wireOp",EDGE,"E70.6.21.0"),sQuery(id+"F15.wireOp",EDGE,"E70.9.21.0"),sQuery(id+"F15.wireOp",EDGE,"E70.12.21.0"),sQuery(id+"F15.wireOp",EDGE,"E70.15.21.0"),sQuery(id+"F15.wireOp",EDGE,"E70.6.22.0"),sQuery(id+"F15.wireOp",EDGE,"E70.9.22.0"),sQuery(id+"F15.wireOp",EDGE,"E70.12.22.0"),sQuery(id+"F15.wireOp",EDGE,"E70.15.22.0"),sQuery(id+"F15.wireOp",EDGE,"E70.6.23.0"),sQuery(id+"F15.wireOp",EDGE,"E70.9.23.0"),sQuery(id+"F15.wireOp",EDGE,"E70.12.23.0"),sQuery(id+"F15.wireOp",EDGE,"E70.15.23.0"),sQuery(id+"F15.wireOp",EDGE,"E68.MirrorCS"),sQuery(id+"F15.wireOp",EDGE,"E66"),sQuery(id+"F15.wireOp",EDGE,"E65"),sQuery(id+"F15.wireOp",EDGE,"E67"),sQuery(id+"F15.wireOp",EDGE,"E71"),sQuery(id+"F15.wireOp",EDGE,"E79.trimOffspring"),sQuery(id+"F15.wireOp",EDGE,"E80.trimOffspring"),sQuery(id+"F15.wireOp",EDGE,"E81.trimOffspring"),sQuery(id+"F15.wireOp",EDGE,"E87.trimOffspring"),sQuery(id+"F15.wireOp",EDGE,"E88.trimOffspring"),sQuery(id+"F15.wireOp",EDGE,"E89.trimOffspring"),sQuery(id+"F15.wireOp",EDGE,"E90.trimOffspring"),sQuery(id+"F15.wireOp",EDGE,"E111.trimOffspring"),sQuery(id+"F15.wireOp",EDGE,"E112.trimOffspring"),sQuery(id+"F15.wireOp",EDGE,"E113.trimOffspring"),sQuery(id+"F15.wireOp",EDGE,"E114.trimOffspring"),sQuery(id+"F15.wireOp",EDGE,"E115.trimOffspring"),sQuery(id+"F15.wireOp",EDGE,"E116.trimOffspring"),sQuery(id+"F15.wireOp",EDGE,"E117.trimOffspring"),sQuery(id+"F15.wireOp",EDGE,"E119.trimOffspring"),sQuery(id+"F15.wireOp",EDGE,"E122.trimOffspring"),sQuery(id+"F15.wireOp",EDGE,"E125.trimOffspring"),sQuery(id+"F15.wireOp",EDGE,"E132.trimOffspring"),sQuery(id+"F15.wireOp",EDGE,"E133.trimOffspring"),sQuery(id+"F15.wireOp",EDGE,"E134.trimOffspring"),sQuery(id+"F15.wireOp",EDGE,"E137.trimOffspring"),sQuery(id+"F15.wireOp",EDGE,"E140"),sQuery(id+"F15.wireOp",EDGE,"E141")])],"isStart":false});
            var sketch = newSketch(context, id + "F17", { "sketchPlane" : qUnion([Q0])});
            skCircle(sketch, "E142", {"center": v(38, 38) * mm, "radius": 7 * mm});
            skSolve(sketch);
        }
        {
            var Q0;
            Q0=makeQuery(id+"F17.imprint","IMPRINT",FACE,{"disambiguationData":[TD([[makeQuery(id+"F17.imprint","IMPRINT",EDGE,{"derivedFrom":sQuery(id+"F17.wireOp",EDGE,"E142")}),1.0]])]});
            extrude(context, id + "F18", {"entities" : qUnion([Q0]), "operationType" : NewBodyOperationType.REMOVE, "oppositeDirection" : true, "depth" : 0.5 * mm});
        }
        {
            var Q0;
            Q0=makeQuery(id+"F18.boolean.opBoolean","COPY",FACE,{"derivedFrom":makeQuery(id+"F18.opExtrude","CAP_FACE",FACE,{"disambiguationData":[OSD([sQuery(id+"F17.wireOp",EDGE,"E142")])],"isStart":false})});
            var sketch = newSketch(context, id + "F19", { "sketchPlane" : qUnion([Q0])});
            skCircle(sketch, "E143", {"center": v(38, 38) * mm, "radius": 2.5 * mm});
            skSolve(sketch);
        }
        {
            var Q0;
            Q0=makeQuery(id+"F19.imprint","IMPRINT",FACE,{"disambiguationData":[TD([[makeQuery(id+"F19.imprint","IMPRINT",EDGE,{"derivedFrom":sQuery(id+"F19.wireOp",EDGE,"E143")}),1.0]])]});
            extrude(context, id + "F20", {"entities" : qUnion([Q0]), "operationType" : NewBodyOperationType.REMOVE, "oppositeDirection" : true, "depth" : 25 * mm});
        }
        {
            var Q0;
            Q0=makeQuery(id+"F1.opExtrude","CAP_FACE",FACE,{"disambiguationData":[OSD([sQuery(id+"F0.wireOp",EDGE,"E11")])],"isStart":true});
            var sketch = newSketch(context, id + "F21", { "sketchPlane" : qUnion([Q0])});
            skCircle(sketch, "E144", {"center": v(38, -38) * mm, "radius": 7 * mm});
            skSolve(sketch);
        }
        {
            var Q0;
            Q0 = qSketchRegion(id + "F21", true);
            extrude(context, id + "F22", {"entities" : qUnion([Q0]), "operationType" : NewBodyOperationType.REMOVE, "oppositeDirection" : true, "depth" : 4 * mm});
        }
        {
            var Q0;
            Q0=makeQuery(id+"F14.boolean.opBoolean","SPLIT",FACE,{"disambiguationData":[TD([makeQuery(id+"F3.opExtrude","SWEPT_FACE",FACE,{"disambiguationData":[OSD([sQuery(id+"F2.wireOp",EDGE,"E15")])]})])],"derivedFrom":makeQuery(id+"F14.opExtrude","CAP_FACE",FACE,{"disambiguationData":[OSD([sQuery(id+"F13.wireOp",EDGE,"E61")])],"isStart":true})});
            var sketch = newSketch(context, id + "F23", { "sketchPlane" : qUnion([Q0])});
            skCircle(sketch, "E145", {"center": v(38, -38) * mm, "radius": 7 * mm});
            skCircle(sketch, "E146", {"center": v(38, -38) * mm, "radius": 2.5 * mm});
            skSolve(sketch);
        }
        {
            var Q0;
            Q0=makeQuery(id+"F23.imprint","IMPRINT",FACE,{"disambiguationData":[TD([[makeQuery(id+"F23.imprint","IMPRINT",EDGE,{"derivedFrom":sQuery(id+"F23.wireOp",EDGE,"E145")}),-1.0]])]});
            extrude(context, id + "F24", {"entities" : qUnion([Q0]), "operationType" : NewBodyOperationType.ADD, "depth" : 3 * mm});
        }
        {
            var Q0;
            Q0=makeQuery(id+"F14.opExtrude","CAP_FACE",FACE,{"disambiguationData":[OSD([sQuery(id+"F13.wireOp",EDGE,"E61")])],"isStart":false});
            var sketch = newSketch(context, id + "F25", { "sketchPlane" : qUnion([Q0])});
            skLineSegment(sketch, "E147", {"start": v(38, 38) * mm, "end": v(38, 15.14) * mm, "construction": true});
            skLineSegment(sketch, "E148", {"start": v(38, 38) * mm, "end": v(60.5, 15.5) * mm, "construction": true});
            skLineSegment(sketch, "E149", {"start": v(38, 38) * mm, "end": v(56.64, 56.64) * mm, "construction": true});
            skLineSegment(sketch, "E150", {"start": v(38, 38) * mm, "end": v(20.24, 55.76) * mm, "construction": true});
            skLineSegment(sketch, "E151", {"start": v(38, 38) * mm, "end": v(16.33, 16.33) * mm, "construction": true});
            skLineSegment(sketch, "E152", {"start": v(53.54, 53.54) * mm, "end": v(50.7, 50.7) * mm, "construction": true});
            skCircle(sketch, "E153", {"center": v(50.7, 50.7) * mm, "radius": 0.75 * mm});
            skCircle(sketch, "E154.MirrorC", {"center": v(25.3, 25.3) * mm, "radius": 0.75 * mm});
            skLineSegment(sketch, "E155", {"start": v(53.54, 22.46) * mm, "end": v(50.7, 25.3) * mm, "construction": true});
            skCircle(sketch, "E156", {"center": v(50.7, 25.3) * mm, "radius": 0.75 * mm});
            skCircle(sketch, "E157.MirrorC", {"center": v(25.3, 50.7) * mm, "radius": 0.75 * mm});
            skSolve(sketch);
        }
        {
            var Q0;
            Q0=makeQuery(id+"F25.imprint","IMPRINT",FACE,{"disambiguationData":[TD([[makeQuery(id+"F25.imprint","IMPRINT",EDGE,{"derivedFrom":sQuery(id+"F25.wireOp",EDGE,"E157.MirrorC")}),-1.0]])]});
            var Q1;
            Q1=makeQuery(id+"F25.imprint","IMPRINT",FACE,{"disambiguationData":[TD([[makeQuery(id+"F25.imprint","IMPRINT",EDGE,{"derivedFrom":sQuery(id+"F25.wireOp",EDGE,"E154.MirrorC")}),-1.0]])]});
            var Q2;
            Q2=makeQuery(id+"F25.imprint","IMPRINT",FACE,{"disambiguationData":[TD([[makeQuery(id+"F25.imprint","IMPRINT",EDGE,{"derivedFrom":sQuery(id+"F25.wireOp",EDGE,"E156")}),1.0]])]});
            var Q3;
            Q3=makeQuery(id+"F25.imprint","IMPRINT",FACE,{"disambiguationData":[TD([[makeQuery(id+"F25.imprint","IMPRINT",EDGE,{"derivedFrom":sQuery(id+"F25.wireOp",EDGE,"E153")}),1.0]])]});
            extrude(context, id + "F26", {"entities" : qUnion([Q0, Q1, Q2, Q3]), "operationType" : NewBodyOperationType.REMOVE, "oppositeDirection" : true, "depth" : 25 * mm});
        }
        {
            var Q0;
            Q0=makeQuery(id+"F14.opExtrude","CAP_FACE",FACE,{"disambiguationData":[OSD([sQuery(id+"F13.wireOp",EDGE,"E61")])],"isStart":false});
            var sketch = newSketch(context, id + "F27", { "sketchPlane" : qUnion([Q0])});
            skLineSegment(sketch, "E158", {"start": v(38, 38) * mm, "end": v(50.7, 25.3) * mm, "construction": true});
            skLineSegment(sketch, "E159", {"start": v(50.7, 25.3) * mm, "end": v(56.9, 19.1) * mm, "construction": true});
            skLineSegment(sketch, "E160", {"start": v(38, 38) * mm, "end": v(55.45, 55.45) * mm, "construction": true});
            skLineSegment(sketch, "E161", {"start": v(38, 38) * mm, "end": v(19.53, 56.47) * mm, "construction": true});
            skLineSegment(sketch, "E162", {"start": v(38, 38) * mm, "end": v(19.78, 19.78) * mm, "construction": true});
            skLineSegment(sketch, "E163", {"start": v(38, 38) * mm, "end": v(50, 38) * mm, "construction": true});
            skLineSegment(sketch, "E164", {"start": v(38, 38) * mm, "end": v(38, 50) * mm, "construction": true});
            skLineSegment(sketch, "E165", {"start": v(38, 38) * mm, "end": v(26, 38) * mm, "construction": true});
            skLineSegment(sketch, "E166", {"start": v(38, 38) * mm, "end": v(38, 26) * mm, "construction": true});
            skFitSpline(sketch, "E167", {"points": [v(53.54, 53.54) * mm, v(38, 50) * mm, v(22.46, 53.54) * mm, v(26, 38) * mm, v(22.46, 22.46) * mm, v(38, 26) * mm, v(53.54, 22.46) * mm, v(50, 38) * mm, v(53.54, 53.54) * mm]});
            skLineSegment(sketch, "E168", {"start": v(50.7, 50.7) * mm, "end": v(48.59, 48.59) * mm, "construction": true});
            skLineSegment(sketch, "E169", {"start": v(53.54, 53.54) * mm, "end": v(58, 49.06) * mm, "construction": true});
            skArc(sketch, "E170", {"start": v(30.96, 51.21) * mm, "mid": v(27.41, 48.59) * mm, "end": v(24.79, 45.04) * mm});
            skArc(sketch, "E171.trimOffspring", {"start": v(51.21, 45.04) * mm, "mid": v(48.59, 48.59) * mm, "end": v(45.04, 51.21) * mm});
            skArc(sketch, "E172.trimOffspring", {"start": v(45.04, 24.79) * mm, "mid": v(48.59, 27.41) * mm, "end": v(51.21, 30.96) * mm});
            skArc(sketch, "E173.trimOffspring", {"start": v(24.79, 30.96) * mm, "mid": v(27.41, 27.41) * mm, "end": v(30.96, 24.79) * mm});
            skCircle(sketch, "E174", {"center": v(50.7, 50.7) * mm, "radius": 0.75 * mm});
            skCircle(sketch, "E175", {"center": v(50.7, 25.3) * mm, "radius": 0.75 * mm});
            skCircle(sketch, "E176", {"center": v(25.3, 25.3) * mm, "radius": 0.75 * mm});
            skCircle(sketch, "E177", {"center": v(25.3, 50.7) * mm, "radius": 0.75 * mm});
            skSolve(sketch);
        }
        {
            var Q0;
            Q0 = qSketchRegion(id + "F27", true);
            extrude(context, id + "F28", {"entities" : qUnion([Q0]), "operationType" : NewBodyOperationType.ADD, "depth" : 0.5 * mm});
        }
        {
            var Q0;
            Q0=qCreatedBy(makeId("Top.planeOp"),FACE);
            var sketch = newSketch(context, id + "F29", { "sketchPlane" : qUnion([Q0])});
            skCircle(sketch, "E178.cCircle", {"center": v(0, 0) * mm, "radius": 5 * mm, "construction": true});
            skLineSegment(sketch, "E178.0", {"start": v(5, 0) * mm, "end": v(2.5, -4.33) * mm});
            skLineSegment(sketch, "E178.1", {"start": v(2.5, -4.33) * mm, "end": v(-2.5, -4.33) * mm});
            skLineSegment(sketch, "E178.2", {"start": v(-2.5, -4.33) * mm, "end": v(-5, 0) * mm});
            skLineSegment(sketch, "E178.3", {"start": v(-5, 0) * mm, "end": v(-2.5, 4.33) * mm});
            skLineSegment(sketch, "E178.4", {"start": v(-2.5, 4.33) * mm, "end": v(2.5, 4.33) * mm});
            skLineSegment(sketch, "E178.5", {"start": v(2.5, 4.33) * mm, "end": v(5, 0) * mm});
            skSolve(sketch);
        }
        {
            var Q0;
            Q0 = qSketchRegion(id + "F29", true);
            extrude(context, id + "F30", {"entities" : qUnion([Q0]), "depth" : 1 * mm});
        }
        {
            var Q0;
            Q0=makeQuery(id+"F30.opExtrude","CAP_FACE",FACE,{"disambiguationData":[OSD([sQuery(id+"F29.wireOp",EDGE,"E178.0"),sQuery(id+"F29.wireOp",EDGE,"E178.1"),sQuery(id+"F29.wireOp",EDGE,"E178.2"),sQuery(id+"F29.wireOp",EDGE,"E178.3"),sQuery(id+"F29.wireOp",EDGE,"E178.4"),sQuery(id+"F29.wireOp",EDGE,"E178.5")])],"isStart":false});
            var sketch = newSketch(context, id + "F31", { "sketchPlane" : qUnion([Q0])});
            skLineSegment(sketch, "E179", {"start": v(0, 4.33) * mm, "end": v(0, 3.83) * mm, "construction": true});
            skLineSegment(sketch, "E180", {"start": v(5, 0) * mm, "end": v(4.5, 0) * mm, "construction": true});
            skLineSegment(sketch, "E181", {"start": v(0, -4.33) * mm, "end": v(0, -3.83) * mm, "construction": true});
            skPoint(sketch, "E181.endSnap0", {"position": v(0, -4.33) * mm});
            skLineSegment(sketch, "E182", {"start": v(-5, 0) * mm, "end": v(-4.5, 0) * mm, "construction": true});
            skLineSegment(sketch, "E183", {"start": v(0, 3.83) * mm, "end": v(0.25, 3.83) * mm});
            skLineSegment(sketch, "E184", {"start": v(0.25, 3.83) * mm, "end": v(0.25, 0.25) * mm});
            skLineSegment(sketch, "E185", {"start": v(0.25, -3.83) * mm, "end": v(-0.25, -3.83) * mm});
            skLineSegment(sketch, "E186", {"start": v(-0.25, -3.83) * mm, "end": v(-0.25, -0.25) * mm});
            skLineSegment(sketch, "E187", {"start": v(-0.25, 3.83) * mm, "end": v(0, 3.83) * mm});
            skLineSegment(sketch, "E188", {"start": v(-4.5, 0) * mm, "end": v(-4.5, 0.25) * mm});
            skLineSegment(sketch, "E189", {"start": v(-4.5, 0.25) * mm, "end": v(-0.25, 0.25) * mm});
            skLineSegment(sketch, "E190", {"start": v(4.5, 0.25) * mm, "end": v(4.5, -0.25) * mm});
            skLineSegment(sketch, "E191", {"start": v(4.5, -0.25) * mm, "end": v(0.25, -0.25) * mm});
            skLineSegment(sketch, "E192", {"start": v(-4.5, -0.25) * mm, "end": v(-4.5, 0) * mm});
            skLineSegment(sketch, "E193.trimOffspring", {"start": v(-0.25, 0.25) * mm, "end": v(-0.25, 3.83) * mm});
            skLineSegment(sketch, "E194.trimOffspring", {"start": v(0.25, 0.25) * mm, "end": v(4.5, 0.25) * mm});
            skLineSegment(sketch, "E195.trimOffspring", {"start": v(0.25, -0.25) * mm, "end": v(0.25, -3.83) * mm});
            skLineSegment(sketch, "E196.trimOffspring", {"start": v(-0.25, -0.25) * mm, "end": v(-4.5, -0.25) * mm});
            skSolve(sketch);
        }
        {
            var Q0;
            Q0=makeQuery(id+"F31.imprint","IMPRINT",FACE,{"disambiguationData":[TD([[makeQuery(id+"F31.imprint","IMPRINT",EDGE,{"derivedFrom":sQuery(id+"F31.wireOp",EDGE,"E183")}),-1.0]])]});
            extrude(context, id + "F32", {"entities" : qUnion([Q0]), "operationType" : NewBodyOperationType.ADD, "depth" : 9 * mm});
        }
        {
            var Q0;
            Q0=makeQuery(id+"F30.opExtrude","CAP_FACE",FACE,{"disambiguationData":[OSD([sQuery(id+"F29.wireOp",EDGE,"E178.0"),sQuery(id+"F29.wireOp",EDGE,"E178.1"),sQuery(id+"F29.wireOp",EDGE,"E178.2"),sQuery(id+"F29.wireOp",EDGE,"E178.3"),sQuery(id+"F29.wireOp",EDGE,"E178.4"),sQuery(id+"F29.wireOp",EDGE,"E178.5")])],"isStart":true});
            var sketch = newSketch(context, id + "F33", { "sketchPlane" : qUnion([Q0])});
            skCircle(sketch, "E197", {"center": v(0, 0) * mm, "radius": 0.5 * mm});
            skSolve(sketch);
        }
        {
            var Q0;
            Q0=makeQuery(id+"F33.imprint","IMPRINT",FACE,{"disambiguationData":[TD([[makeQuery(id+"F33.imprint","IMPRINT",EDGE,{"derivedFrom":sQuery(id+"F33.wireOp",EDGE,"E197")}),1.0]])]});
            extrude(context, id + "F34", {"entities" : qUnion([Q0]), "operationType" : NewBodyOperationType.REMOVE, "oppositeDirection" : true, "depth" : 25 * mm});
        }
        {
            var Q0;
            Q0=makeQuery(id+"F32.opExtrude","SWEPT_FACE",FACE,{"disambiguationData":[OSD([sQuery(id+"F31.wireOp",EDGE,"E196.trimOffspring")])]});
            var sketch = newSketch(context, id + "F35", { "sketchPlane" : qUnion([Q0])});
            skLineSegment(sketch, "E198", {"start": v(-4.5, 1) * mm, "end": v(-0.43, 10) * mm});
            skLineSegment(sketch, "E199", {"start": v(-0.43, 10) * mm, "end": v(-4.5, 10) * mm});
            skLineSegment(sketch, "E200", {"start": v(-4.5, 10) * mm, "end": v(-4.5, 1) * mm});
            skSolve(sketch);
        }
        {
            var Q0;
            Q0=makeQuery(id+"F35.imprint","IMPRINT",FACE,{"disambiguationData":[TD([[makeQuery(id+"F35.imprint","IMPRINT",EDGE,{"derivedFrom":sQuery(id+"F35.wireOp",EDGE,"E198")}),1.0]])]});
            extrude(context, id + "F36", {"entities" : qUnion([Q0]), "operationType" : NewBodyOperationType.REMOVE, "oppositeDirection" : true, "depth" : 25 * mm});
        }
        {
            var Q0;
            Q0=makeQuery(id+"F32.opExtrude","SWEPT_FACE",FACE,{"disambiguationData":[OSD([sQuery(id+"F31.wireOp",EDGE,"E191")])]});
            var sketch = newSketch(context, id + "F37", { "sketchPlane" : qUnion([Q0])});
            skLineSegment(sketch, "E201", {"start": v(4.5, 1) * mm, "end": v(0.43, 10) * mm});
            skLineSegment(sketch, "E202", {"start": v(0.43, 10) * mm, "end": v(4.5, 10) * mm});
            skLineSegment(sketch, "E203", {"start": v(4.5, 10) * mm, "end": v(4.5, 1) * mm});
            skSolve(sketch);
        }
        {
            var Q0;
            Q0=makeQuery(id+"F37.imprint","IMPRINT",FACE,{"disambiguationData":[TD([[makeQuery(id+"F37.imprint","IMPRINT",EDGE,{"derivedFrom":sQuery(id+"F37.wireOp",EDGE,"E201")}),-1.0]])]});
            extrude(context, id + "F38", {"entities" : qUnion([Q0]), "operationType" : NewBodyOperationType.REMOVE, "oppositeDirection" : true, "depth" : 25 * mm});
        }
        {
            var Q0;
            Q0=makeQuery(id+"F32.opExtrude","SWEPT_FACE",FACE,{"disambiguationData":[OSD([sQuery(id+"F31.wireOp",EDGE,"E195.trimOffspring")])]});
            var sketch = newSketch(context, id + "F39", { "sketchPlane" : qUnion([Q0])});
            skLineSegment(sketch, "E204", {"start": v(-3.83, 1) * mm, "end": v(-0.43, 10) * mm});
            skLineSegment(sketch, "E205", {"start": v(-0.43, 10) * mm, "end": v(-3.83, 10) * mm});
            skLineSegment(sketch, "E206", {"start": v(-3.83, 10) * mm, "end": v(-3.83, 1) * mm});
            skSolve(sketch);
        }
        {
            var Q0;
            Q0 = qSketchRegion(id + "F39", true);
            extrude(context, id + "F40", {"entities" : qUnion([Q0]), "operationType" : NewBodyOperationType.REMOVE, "oppositeDirection" : true, "depth" : 25 * mm});
        }
        {
            var Q0;
            Q0=makeQuery(id+"F32.opExtrude","SWEPT_FACE",FACE,{"disambiguationData":[OSD([sQuery(id+"F31.wireOp",EDGE,"E184")])]});
            var sketch = newSketch(context, id + "F41", { "sketchPlane" : qUnion([Q0])});
            skLineSegment(sketch, "E207", {"start": v(3.83, 1) * mm, "end": v(0.43, 10) * mm});
            skLineSegment(sketch, "E208", {"start": v(0.43, 10) * mm, "end": v(3.83, 10) * mm});
            skLineSegment(sketch, "E209", {"start": v(3.83, 10) * mm, "end": v(3.83, 1) * mm});
            skSolve(sketch);
        }
        {
            var Q0;
            Q0 = qSketchRegion(id + "F41", true);
            extrude(context, id + "F42", {"entities" : qUnion([Q0]), "operationType" : NewBodyOperationType.REMOVE, "oppositeDirection" : true, "depth" : 25 * mm});
        }
        {
            var Q0;
            Q0=makeQuery(id+"F32.opExtrude","SWEPT_FACE",FACE,{"disambiguationData":[OSD([sQuery(id+"F31.wireOp",EDGE,"E196.trimOffspring")])]});
            var sketch = newSketch(context, id + "F43", { "sketchPlane" : qUnion([Q0])});
            skLineSegment(sketch, "E210", {"start": v(-0.43, 1) * mm, "end": v(-0.43, 8) * mm, "construction": true});
            skLineSegment(sketch, "E211", {"start": v(-0.43, 8) * mm, "end": v(-1.34, 8) * mm});
            skSolve(sketch);
        }
        {
            var Q0;
            {var subQ0=sQuery(id+"F43.wireOp",EDGE,"E211");Q0=makeQuery(id+"F43.imprint","IMPRINT",FACE,{"disambiguationData":[TD([[makeQuery(id+"F43.imprint","IMPRINT",EDGE,{"derivedFrom":subQ0}),-1.0]])]});}
            extrude(context, id + "F44", {"entities" : qUnion([Q0]), "operationType" : NewBodyOperationType.REMOVE, "oppositeDirection" : true, "depth" : 25 * mm});
        }
        {
            var Q0;
            Q0=makeQuery(id+"F32.opExtrude","SWEPT_FACE",FACE,{"disambiguationData":[OSD([sQuery(id+"F31.wireOp",EDGE,"E191")])]});
            var sketch = newSketch(context, id + "F45", { "sketchPlane" : qUnion([Q0])});
            skLineSegment(sketch, "E212", {"start": v(0.43, 1) * mm, "end": v(0.43, 8) * mm, "construction": true});
            skLineSegment(sketch, "E213", {"start": v(0.43, 8) * mm, "end": v(1.34, 8) * mm});
            skSolve(sketch);
        }
        {
            var Q0;
            {var subQ0=sQuery(id+"F45.wireOp",EDGE,"E213");Q0=makeQuery(id+"F45.imprint","IMPRINT",FACE,{"disambiguationData":[TD([[makeQuery(id+"F45.imprint","IMPRINT",EDGE,{"derivedFrom":subQ0}),1.0]])]});}
            extrude(context, id + "F46", {"entities" : qUnion([Q0]), "operationType" : NewBodyOperationType.REMOVE, "oppositeDirection" : true, "depth" : 25 * mm});
        }
        {
            var Q0;
            Q0=makeQuery(id+"F32.opExtrude","SWEPT_FACE",FACE,{"disambiguationData":[OSD([sQuery(id+"F31.wireOp",EDGE,"E195.trimOffspring")])]});
            var sketch = newSketch(context, id + "F47", { "sketchPlane" : qUnion([Q0])});
            skLineSegment(sketch, "E214", {"start": v(-0.43, 1) * mm, "end": v(-0.43, 8) * mm, "construction": true});
            skLineSegment(sketch, "E215", {"start": v(-0.43, 8) * mm, "end": v(-1.19, 8) * mm});
            skSolve(sketch);
        }
        {
            var Q0;
            {var subQ0=sQuery(id+"F47.wireOp",EDGE,"E215");Q0=makeQuery(id+"F47.imprint","IMPRINT",FACE,{"disambiguationData":[TD([[makeQuery(id+"F47.imprint","IMPRINT",EDGE,{"derivedFrom":subQ0}),-1.0]])]});}
            extrude(context, id + "F48", {"entities" : qUnion([Q0]), "operationType" : NewBodyOperationType.REMOVE, "oppositeDirection" : true, "depth" : 25 * mm});
        }
        {
            var Q0;
            Q0=makeQuery(id+"F32.opExtrude","SWEPT_FACE",FACE,{"disambiguationData":[OSD([sQuery(id+"F31.wireOp",EDGE,"E184")])]});
            var sketch = newSketch(context, id + "F49", { "sketchPlane" : qUnion([Q0])});
            skLineSegment(sketch, "E216", {"start": v(0.43, 1) * mm, "end": v(0.43, 8) * mm, "construction": true});
            skLineSegment(sketch, "E217", {"start": v(0.43, 8) * mm, "end": v(1.19, 8) * mm});
            skSolve(sketch);
        }
        {
            var Q0;
            {var subQ0=sQuery(id+"F49.wireOp",EDGE,"E217");Q0=makeQuery(id+"F49.imprint","IMPRINT",FACE,{"disambiguationData":[TD([[makeQuery(id+"F49.imprint","IMPRINT",EDGE,{"derivedFrom":subQ0}),1.0]])]});}
            extrude(context, id + "F50", {"entities" : qUnion([Q0]), "operationType" : NewBodyOperationType.REMOVE, "oppositeDirection" : true, "depth" : 25 * mm});
        }
        {
            var Q0;
            Q0=makeQuery(id+"F30.opExtrude","CAP_FACE",FACE,{"disambiguationData":[OSD([sQuery(id+"F29.wireOp",EDGE,"E178.0"),sQuery(id+"F29.wireOp",EDGE,"E178.1"),sQuery(id+"F29.wireOp",EDGE,"E178.2"),sQuery(id+"F29.wireOp",EDGE,"E178.3"),sQuery(id+"F29.wireOp",EDGE,"E178.4"),sQuery(id+"F29.wireOp",EDGE,"E178.5")])],"isStart":true});
            var sketch = newSketch(context, id + "F51", { "sketchPlane" : qUnion([Q0])});
            skCircle(sketch, "E218", {"center": v(0, 0) * mm, "radius": 1 * mm});
            skSolve(sketch);
        }
        {
            var Q0;
            Q0=makeQuery(id+"F51.imprint","IMPRINT",FACE,{"disambiguationData":[TD([[makeQuery(id+"F51.imprint","IMPRINT",EDGE,{"derivedFrom":sQuery(id+"F51.wireOp",EDGE,"E218")}),1.0]])]});
            extrude(context, id + "F52", {"entities" : qUnion([Q0]), "operationType" : NewBodyOperationType.REMOVE, "oppositeDirection" : true, "depth" : 0.6 * mm});
        }
    });
